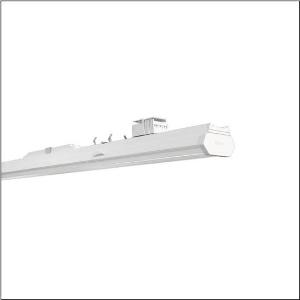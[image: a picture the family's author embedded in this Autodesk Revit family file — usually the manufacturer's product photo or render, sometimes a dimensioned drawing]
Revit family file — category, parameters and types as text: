
# Revit family: licross_r__11_protected_mo_51tp127n485g_ff31
name_source: partatom
category: Lighting Fixtures
units: mm (PartAtom-declared; Revit-internal decimal feet)

## family parameters
Cut with Voids When Loaded = No
Host = Face
Light Source = No
Part Type = Normal
Room Calculation Point = No
Round Connector Dimension = Use Diameter
Shared = No

## types (1)
- Licross® 11 Protected MO (1 x LED, 8720 lm, 48.6 W, 4000K)
    Apparent Load = 49 VA
    CIE Flux Codes = 73 92 98 99 100
    Color Rendering = 80
    Color Temperature = 4000K
    Default Elevation = 1800 mm
    Description = Licross® 11 Protected MO, luminaire insert, of sheet steel, galvanised, coil coated, white, length: 1.500mm, width: 90mm, height: 101mm, LED rated luminous flux: 8.720lm, light colour: 840, control gear: ON/OFF, with plug, 3-pole, with phase selection, mains connection: 220..240V, AC, 50/60Hz, rated input power: 49W, halogen-free wiring, primary light control with lens, of plastic, primary optical cover: cover, of PMMA, light emission: direct distribution, primary light characteristic: symmetric, protection rating (complete): IP64, insulation class (complete): insulation class I (protective earthing), certification: CE, ENEC, VDE, UKCA, protection symbol: D if used in an environment with conductive dust loads with corresponding accessories, impact resistance: IK06, permissible ambient temperature for indoor applications: -25..+35°C, corresponds to IFS (International Featured Standards) requirements for safety and quality in the food industry, reducing of maximum allowable ambient temperature of 5°C with ceiling mounting, LABS conformity tested according to VDMA 24364:2018-05, packaging unit: 1 piece
    Height = 92 mm
    Lamp = 1 x LED
    Lamp Light Flux = 8720 lm
    Lamp Power = 48.6 W
    Lamp count = 1
    Length = 1500 mm
    Luminous efficacy = 179 lm/W
    Manufacturer = Siteco
    ModVariant = No
    Model = 51TP127N485G
    Mounting Place = Ceiling
    Mounting Type = Pendant
    Number of Poles = 1
    OnlyDefault = Yes
    Power Factor = 1
    Product Name = Licross® 11 Protected MO
    Product group = luminaire insert
    ProductGroupID = 901
    Protection Class = Protection class I
    Protection Degree = IP 64
    RLX_Detail_Level = 1
    RLX_Emergency_Light_Flux = 0 lm
    RLX_Emergency_Type = 0
    RLX_Emergency_Type_DB = No
    RlxData = <blob elided: 20637 chars, md5=f221bb04>
    Socket = socket
    Standby Power = 0 W
    System Light Flux = 8720 lm
    System Power = 49 W
    Type Comments = Product without accessories
    Type Image = l_1256148.jpg
    URL = http://relux.com
    VarID = ---
    Voltage = 0 V
    Weight = 0.00 kg
    Width = 88 mm

## geometry (parser evidence)
native form markers: Blend x4, Sweep x11
no freeform markers — native parametric forms only
